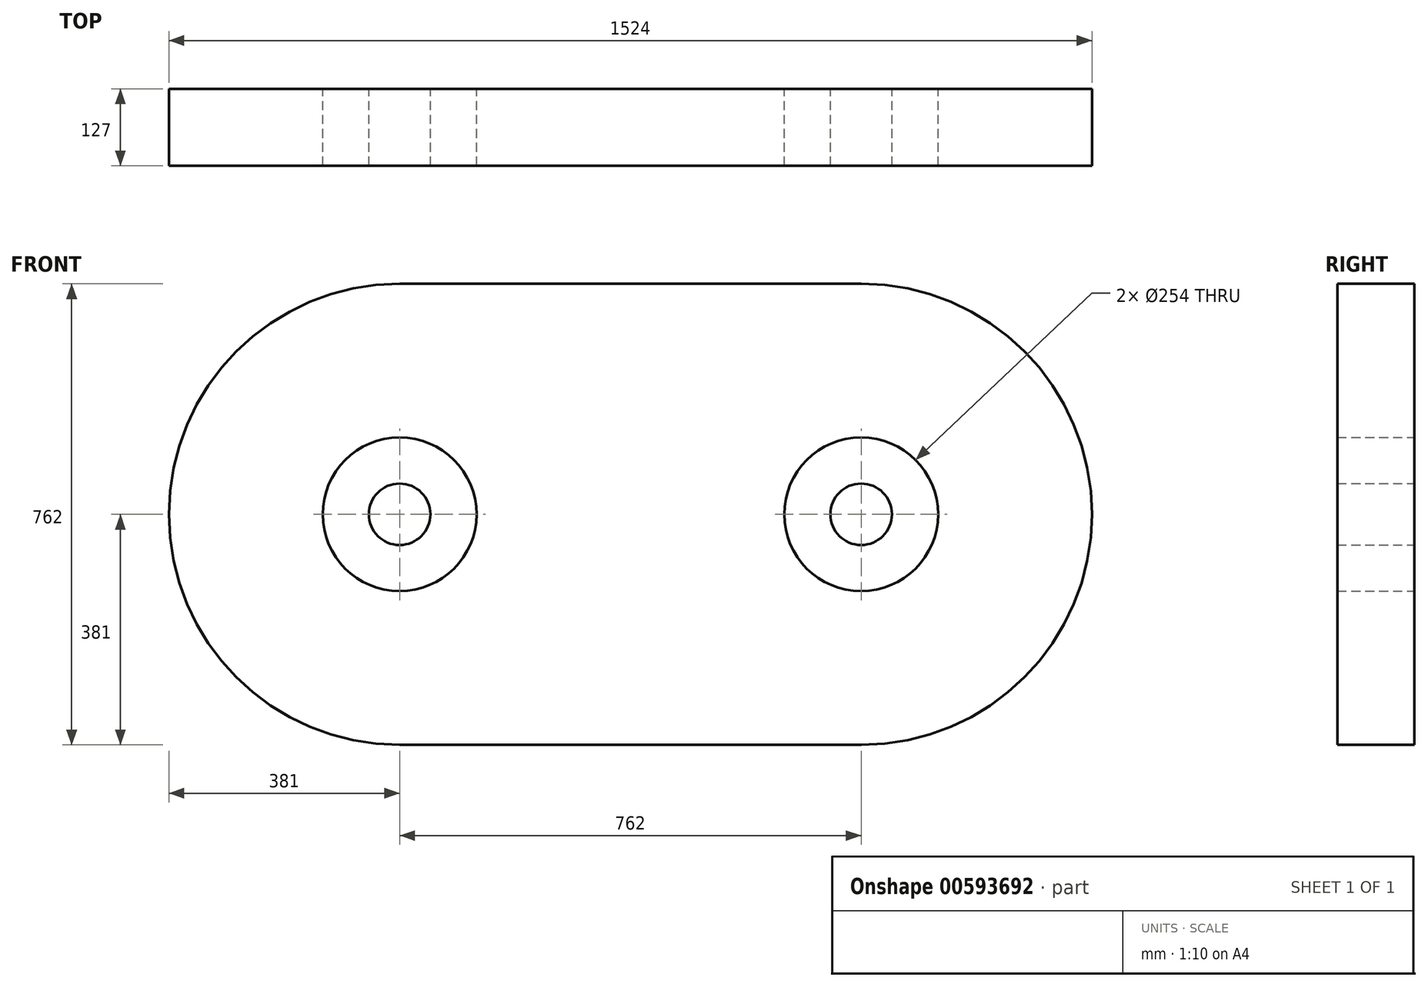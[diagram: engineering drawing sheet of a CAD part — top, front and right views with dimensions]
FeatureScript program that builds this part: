
annotation { "Feature Type Name" : "Feature", "Feature Type Description" : "" }
export const myFeature = defineFeature(function(context is Context, id is Id, definition is map)
    precondition{}
    {
        {
            var Q0;
            Q0=qCreatedBy(makeId("Front.planeOp"),FACE);
            var sketch = newSketch(context, id + "F0", { "sketchPlane" : qUnion([Q0])});
            skLineSegment(sketch, "E0.bottom", {"start": v(-381, 381) * mm, "end": v(381, 381) * mm});
            skLineSegment(sketch, "E0.top", {"start": v(-381, -381) * mm, "end": v(381, -381) * mm});
            skLineSegment(sketch, "E0.left", {"start": v(-381, 381) * mm, "end": v(-381, -381) * mm, "construction": true});
            skLineSegment(sketch, "E0.right", {"start": v(381, 381) * mm, "end": v(381, -381) * mm, "construction": true});
            skArc(sketch, "E1", {"start": v(-381, 381) * mm, "mid": v(-762, 0) * mm, "end": v(-381, -381) * mm});
            skArc(sketch, "E2.MirrorCS", {"start": v(381, 381) * mm, "mid": v(762, 0) * mm, "end": v(381, -381) * mm});
            skCircle(sketch, "E3", {"center": v(-381, 0) * mm, "radius": 127 * mm});
            skCircle(sketch, "E4", {"center": v(381, 0) * mm, "radius": 127 * mm});
            skCircle(sketch, "E5", {"center": v(-381, 0) * mm, "radius": 50.8 * mm});
            skCircle(sketch, "E6", {"center": v(381, 0) * mm, "radius": 50.8 * mm});
            skSolve(sketch);
        }
        {
            var Q0;
            Q0 = qSketchRegion(id + "F0", true);
            var Q1;
            Q1=makeQuery(id+"F0.imprint","IMPRINT",FACE,{"disambiguationData":[TD([[makeQuery(id+"F0.imprint","IMPRINT",EDGE,{"derivedFrom":sQuery(id+"F0.wireOp",EDGE,"E5")}),1.0]])]});
            var Q2;
            Q2=makeQuery(id+"F0.imprint","IMPRINT",FACE,{"disambiguationData":[TD([[makeQuery(id+"F0.imprint","IMPRINT",EDGE,{"derivedFrom":sQuery(id+"F0.wireOp",EDGE,"E6")}),1.0]])]});
            extrude(context, id + "F1", {"entities" : qUnion([Q0, Q1, Q2]), "depth" : 127 * mm, "offsetDistance" : 25.4 * mm});
        }
    });
